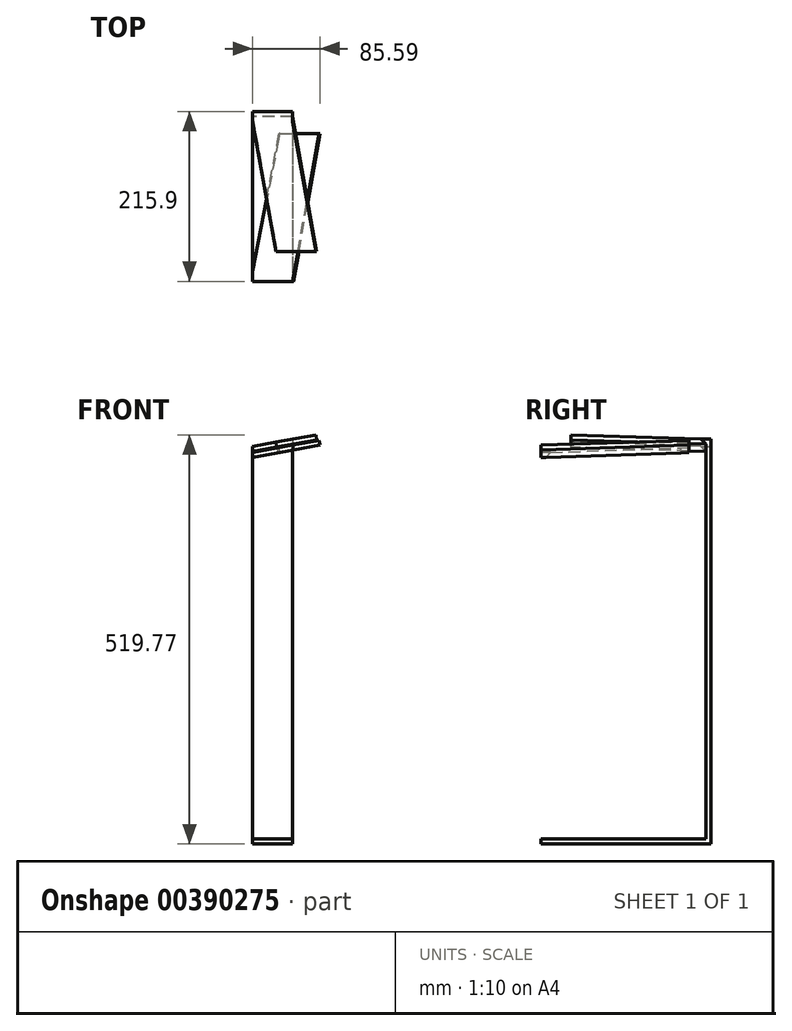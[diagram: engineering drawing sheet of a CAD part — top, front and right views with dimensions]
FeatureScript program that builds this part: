
annotation { "Feature Type Name" : "Feature", "Feature Type Description" : "" }
export const myFeature = defineFeature(function(context is Context, id is Id, definition is map)
    precondition{}
    {
        {
            var Q0;
            Q0=qCreatedBy(makeId("Front.planeOp"),FACE);
            var sketch = newSketch(context, id + "F0", { "sketchPlane" : qUnion([Q0])});
            skLineSegment(sketch, "E0.bottom", {"start": v(-25.4, 254) * mm, "end": v(25.4, 254) * mm});
            skLineSegment(sketch, "E0.top", {"start": v(-25.4, -254) * mm, "end": v(25.4, -254) * mm});
            skLineSegment(sketch, "E0.left", {"start": v(-25.4, 254) * mm, "end": v(-25.4, -254) * mm});
            skLineSegment(sketch, "E0.right", {"start": v(25.4, 254) * mm, "end": v(25.4, -254) * mm});
            skPoint(sketch, "E0.middle", {"position": v(0, 0) * mm});
            skLineSegment(sketch, "E1.left", {"start": v(-25.4, -254) * mm, "end": v(-25.4, -247.65) * mm});
            skLineSegment(sketch, "E1.right", {"start": v(25.4, -254) * mm, "end": v(25.4, -247.65) * mm});
            skLineSegment(sketch, "E2.top", {"start": v(-25.4, -260.35) * mm, "end": v(25.4, -260.35) * mm});
            skLineSegment(sketch, "E2.left", {"start": v(-25.4, -254) * mm, "end": v(-25.4, -260.35) * mm});
            skLineSegment(sketch, "E2.right", {"start": v(25.4, -254) * mm, "end": v(25.4, -260.35) * mm});
            skLineSegment(sketch, "E3", {"start": v(-25.4, 230.77) * mm, "end": v(25.4, 240) * mm});
            skLineSegment(sketch, "E4", {"start": v(-25.4, 237.22) * mm, "end": v(25.4, 246.46) * mm});
            skSolve(sketch);
        }
        {
            var Q0;
            {var subQ0=sQuery(id+"F0.wireOp",EDGE,"E1.left");Q0=makeQuery(id+"F0.imprint","IMPRINT",FACE,{"disambiguationData":[TD([[makeQuery(id+"F0.imprint","IMPRINT",EDGE,{"derivedFrom":subQ0}),-1.0]])]});}
            var Q1;
            {var subQ0=sQuery(id+"F0.wireOp",EDGE,"E3");Q1=makeQuery(id+"F0.imprint","IMPRINT",FACE,{"disambiguationData":[TD([[makeQuery(id+"F0.imprint","IMPRINT",EDGE,{"derivedFrom":subQ0}),1.0]])]});}
            extrude(context, id + "F1", {"entities" : qUnion([Q0, Q1]), "oppositeDirection" : true, "depth" : 6.35 * mm, "offsetDistance" : 25.4 * mm});
        }
        {
            var Q0;
            Q0=makeQuery(id+"F0.imprint","IMPRINT",FACE,{"disambiguationData":[TD([[makeQuery(id+"F0.imprint","IMPRINT",EDGE,{"derivedFrom":sQuery(id+"F0.wireOp",EDGE,"E0.top")}),-1.0]])]});
            extrude(context, id + "F2", {"entities" : qUnion([Q0]), "operationType" : NewBodyOperationType.ADD, "oppositeDirection" : true, "depth" : 215.9 * mm, "offsetDistance" : 25.4 * mm});
        }
        {
            var Q0;
            Q0=makeQuery(id+"F2.opExtrude","SWEPT_FACE",FACE,{"disambiguationData":[OSD([sQuery(id+"F0.wireOp",EDGE,"E2.top")])]});
            var sketch = newSketch(context, id + "F3", { "sketchPlane" : qUnion([Q0])});
            skLineSegment(sketch, "E5.bottom", {"start": v(25.4, -215.9) * mm, "end": v(-25.4, -215.9) * mm});
            skLineSegment(sketch, "E5.top", {"start": v(25.4, -209.55) * mm, "end": v(-25.4, -209.55) * mm});
            skLineSegment(sketch, "E5.left", {"start": v(25.4, -215.9) * mm, "end": v(25.4, -209.55) * mm});
            skLineSegment(sketch, "E5.right", {"start": v(-25.4, -215.9) * mm, "end": v(-25.4, -209.55) * mm});
            skSolve(sketch);
        }
        {
            var Q0;
            Q0=makeQuery(id+"F3.imprint","IMPRINT",FACE,{"disambiguationData":[TD([[makeQuery(id+"F3.imprint","IMPRINT",EDGE,{"derivedFrom":sQuery(id+"F3.wireOp",EDGE,"E5.bottom")}),1.0]])]});
            extrude(context, id + "F4", {"entities" : qUnion([Q0]), "operationType" : NewBodyOperationType.ADD, "oppositeDirection" : true, "depth" : 558.8 * mm, "offsetDistance" : 25.4 * mm});
        }
        {
            var Q0;
            {var subQ0=sQuery(id+"F0.wireOp",EDGE,"E3");Q0=makeQuery(id+"F0.imprint","IMPRINT",FACE,{"disambiguationData":[TD([[makeQuery(id+"F0.imprint","IMPRINT",EDGE,{"derivedFrom":subQ0}),1.0]])]});}
            extrude(context, id + "F5", {"entities" : qUnion([Q0]), "operationType" : NewBodyOperationType.ADD, "oppositeDirection" : true, "depth" : 177.8 * mm, "offsetDistance" : 25.4 * mm});
        }
        {
            var Q0;
            Q0=makeQuery(id+"F4.boolean.opBoolean","MERGE",FACE,{"derivedFrom":[makeQuery(id+"F2.opExtrude","CAP_FACE",FACE,{"disambiguationData":[OSD([sQuery(id+"F0.wireOp",EDGE,"E0.top"),sQuery(id+"F0.wireOp",EDGE,"E2.top"),sQuery(id+"F0.wireOp",EDGE,"E2.left"),sQuery(id+"F0.wireOp",EDGE,"E2.right")])],"isStart":false}),makeQuery(id+"F4.opExtrude","SWEPT_FACE",FACE,{"disambiguationData":[OSD([sQuery(id+"F3.wireOp",EDGE,"E5.bottom")])]})]});
            var sketch = newSketch(context, id + "F6", { "sketchPlane" : qUnion([Q0])});
            skLineSegment(sketch, "E6", {"start": v(25.4, 238.5) * mm, "end": v(-25.4, 247.65) * mm});
            skLineSegment(sketch, "E7", {"start": v(-25.4, 254.1) * mm, "end": v(25.4, 244.96) * mm});
            skSolve(sketch);
        }
        {
            var Q0;
            {var subQ0=sQuery(id+"F6.wireOp",EDGE,"E7");Q0=makeQuery(id+"F6.imprint","IMPRINT",FACE,{"disambiguationData":[TD([[makeQuery(id+"F6.imprint","IMPRINT",EDGE,{"derivedFrom":subQ0}),1.0]])]});}
            extrude(context, id + "F7", {"entities" : qUnion([Q0]), "operationType" : NewBodyOperationType.REMOVE, "oppositeDirection" : true, "depth" : 6.35 * mm, "offsetDistance" : 25.4 * mm});
        }
        {
            var Q0;
            {var subQ0=sQuery(id+"F6.wireOp",EDGE,"E6");Q0=makeQuery(id+"F6.imprint","IMPRINT",FACE,{"disambiguationData":[TD([[makeQuery(id+"F6.imprint","IMPRINT",EDGE,{"derivedFrom":subQ0}),-1.0]])]});}
            extrude(context, id + "F8", {"entities" : qUnion([Q0]), "operationType" : NewBodyOperationType.ADD, "oppositeDirection" : true, "depth" : 177.8 * mm, "offsetDistance" : 25.4 * mm});
        }
        {
            var Q0;
            {var subQ0=sQuery(id+"F0.wireOp",EDGE,"E4");Q0=makeQuery(id+"F5.boolean.opBoolean","MERGE",FACE,{"derivedFrom":[makeQuery(id+"F1.opExtrude","SWEPT_FACE",FACE,{"disambiguationData":[OSD([subQ0])]}),makeQuery(id+"F5.opExtrude","SWEPT_FACE",FACE,{"disambiguationData":[OSD([subQ0])]})]});}
            var sketch = newSketch(context, id + "F9", { "sketchPlane" : qUnion([Q0])});
            skLineSegment(sketch, "E8", {"start": v(17.46, 0) * mm, "end": v(60.2, 234.98) * mm});
            skLineSegment(sketch, "E9", {"start": v(69.1, 0) * mm, "end": v(111.47, 232.96) * mm});
            skLineSegment(sketch, "E10", {"start": v(111.47, 232.96) * mm, "end": v(60.2, 232.96) * mm});
            skLineSegment(sketch, "E11", {"start": v(51.67, 188.07) * mm, "end": v(103.3, 188.07) * mm});
            skLineSegment(sketch, "E12", {"start": v(51.67, 188.07) * mm, "end": v(16.81, 188.07) * mm});
            skSolve(sketch);
        }
        {
            var Q0;
            Q0 = qSketchRegion(id + "F9", true);
            var Q1;
            {var subQ1=sQuery(id+"F0.wireOp",EDGE,"E4");var subQ3=makeQuery(id+"F1.opExtrude","CAP_EDGE",EDGE,{"disambiguationData":[OSD([subQ1])],"isStart":true});Q1=makeQuery(id+"F9.imprint","IMPRINT",FACE,{"disambiguationData":[TD([[makeQuery(id+"F9.imprint","IMPRINT",EDGE,{"derivedFrom":subQ3}),1.0]])]});}
            var Q2;
            {var subQ0=sQuery(id+"F9.wireOp",EDGE,"E11");Q2=makeQuery(id+"F9.imprint","IMPRINT",FACE,{"disambiguationData":[TD([[makeQuery(id+"F9.imprint","IMPRINT",EDGE,{"derivedFrom":subQ0}),-1.0]])]});}
            extrude(context, id + "F10", {"entities" : qUnion([Q0, Q1, Q2]), "operationType" : NewBodyOperationType.ADD, "oppositeDirection" : true, "depth" : 6.35 * mm, "offsetDistance" : 25.4 * mm});
        }
        {
            var Q0;
            Q0=makeQuery(id+"F10.boolean.opBoolean","MERGE",FACE,{"derivedFrom":[makeQuery(id+"F5.opExtrude","SWEPT_FACE",FACE,{"disambiguationData":[OSD([sQuery(id+"F0.wireOp",EDGE,"E3")])]}),makeQuery(id+"F10.opExtrude","CAP_FACE",FACE,{"disambiguationData":[OSD([sQuery(id+"F0.wireOp",EDGE,"E4"),sQuery(id+"F9.wireOp",EDGE,"E8"),sQuery(id+"F9.wireOp",EDGE,"E9"),sQuery(id+"F9.wireOp",EDGE,"E11")])],"isStart":false})]});
            var sketch = newSketch(context, id + "F11", { "sketchPlane" : qUnion([Q0])});
            skLineSegment(sketch, "E13", {"start": v(16.3, -6.35) * mm, "end": v(49.8, -177.8) * mm});
            skLineSegment(sketch, "E14", {"start": v(49.8, -177.8) * mm, "end": v(16.3, -177.8) * mm});
            skLineSegment(sketch, "E15", {"start": v(16.3, -177.8) * mm, "end": v(16.3, -6.35) * mm});
            skSolve(sketch);
        }
        {
            var Q0;
            Q0 = qSketchRegion(id + "F11", true);
            extrude(context, id + "F12", {"entities" : qUnion([Q0]), "operationType" : NewBodyOperationType.REMOVE, "oppositeDirection" : true, "depth" : 6.35 * mm, "offsetDistance" : 25.4 * mm});
        }
        {
            var Q0;
            Q0=makeQuery(id+"F8.opExtrude","SWEPT_FACE",FACE,{"disambiguationData":[OSD([sQuery(id+"F6.wireOp",EDGE,"E6")])]});
            var sketch = newSketch(context, id + "F13", { "sketchPlane" : qUnion([Q0])});
            skLineSegment(sketch, "E16", {"start": v(17.25, -209.55) * mm, "end": v(48.44, -38.1) * mm});
            skLineSegment(sketch, "E17", {"start": v(68.87, -209.55) * mm, "end": v(102.06, -27.06) * mm});
            skLineSegment(sketch, "E18", {"start": v(48.44, -38.1) * mm, "end": v(100.06, -38.1) * mm});
            skLineSegment(sketch, "E19", {"start": v(48.44, -38.1) * mm, "end": v(17.25, -38.1) * mm});
            skLineSegment(sketch, "E20", {"start": v(17.25, -38.1) * mm, "end": v(17.25, -209.55) * mm});
            skSolve(sketch);
        }
        {
            var Q0;
            {var subQ1=sQuery(id+"F6.wireOp",EDGE,"E6");var subQ2=makeQuery(id+"F8.opExtrude","SWEPT_EDGE",EDGE,{"disambiguationData":[OSD([sQuery(id+"F0.wireOp",EDGE,"E2.right"),sQuery(id+"F3.wireOp",EDGE,"E5.bottom"),sQuery(id+"F3.wireOp",EDGE,"E5.left"),subQ1])]});Q0=makeQuery(id+"F13.imprint","IMPRINT",FACE,{"disambiguationData":[TD([[makeQuery(id+"F13.imprint","IMPRINT",EDGE,{"derivedFrom":subQ2}),1.0]])]});}
            extrude(context, id + "F14", {"entities" : qUnion([Q0]), "operationType" : NewBodyOperationType.ADD, "oppositeDirection" : true, "depth" : 6.35 * mm, "offsetDistance" : 25.4 * mm});
        }
        {
            var Q0;
            Q0 = qSketchRegion(id + "F13", true);
            extrude(context, id + "F15", {"entities" : qUnion([Q0]), "operationType" : NewBodyOperationType.REMOVE, "oppositeDirection" : true, "depth" : 6.35 * mm, "offsetDistance" : 25.4 * mm});
        }
    });
